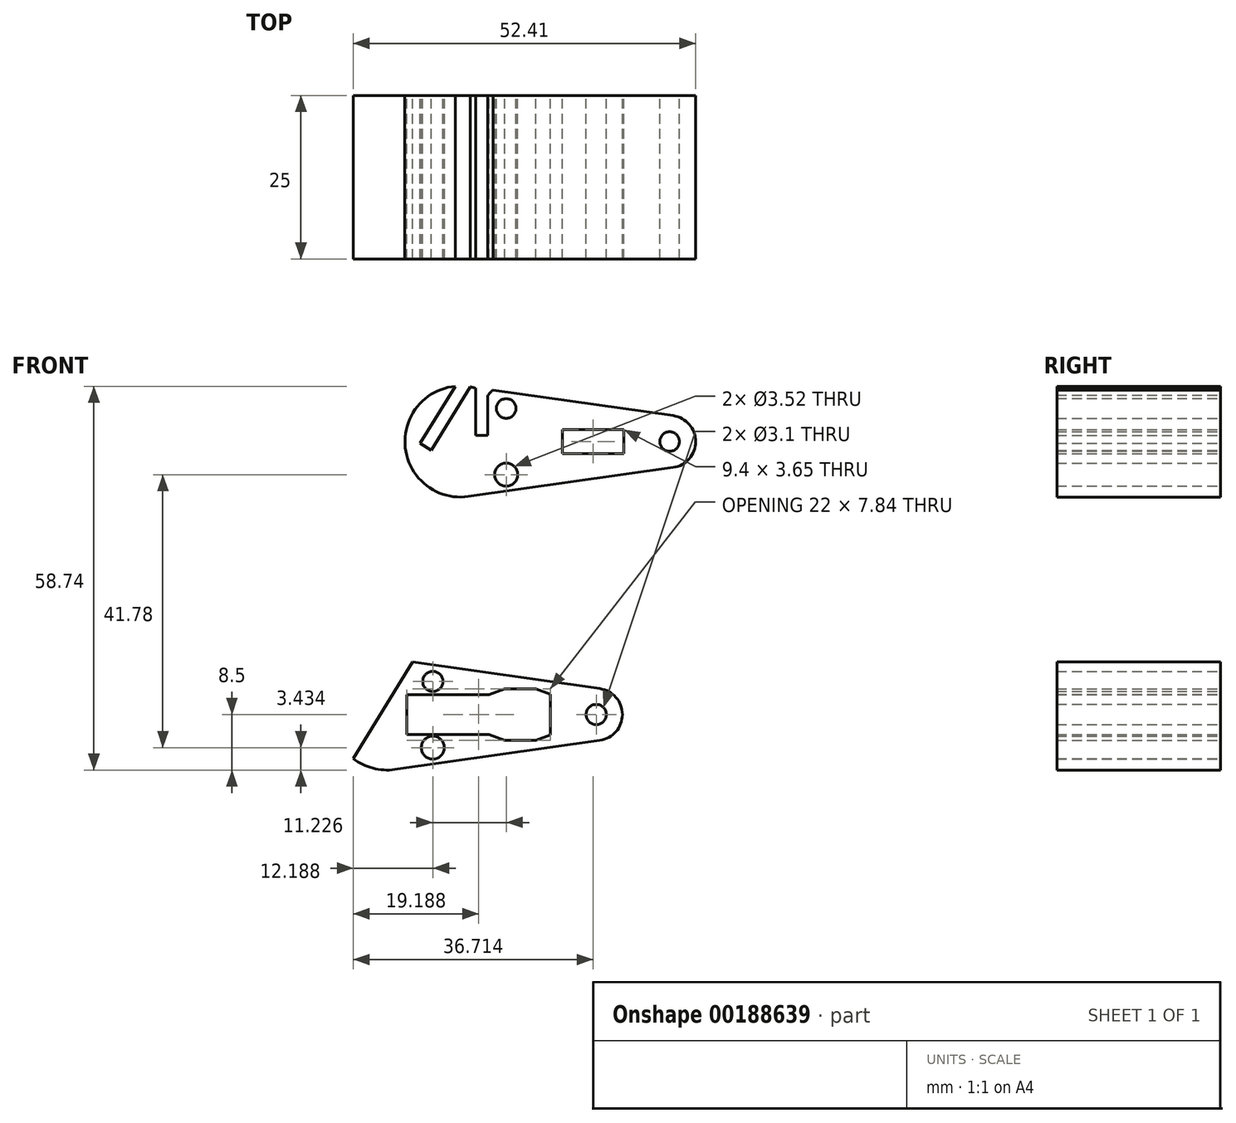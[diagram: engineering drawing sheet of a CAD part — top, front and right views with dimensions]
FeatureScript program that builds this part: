
annotation { "Feature Type Name" : "Feature", "Feature Type Description" : "" }
export const myFeature = defineFeature(function(context is Context, id is Id, definition is map)
    precondition{}
    {
        {
            var Q0;
            Q0=qCreatedBy(makeId("Front.planeOp"),FACE);
            var sketch = newSketch(context, id + "F0", { "sketchPlane" : qUnion([Q0])});
            skCircle(sketch, "E0", {"center": v(-54.37, 44.88) * mm, "radius": 8.5 * mm});
            skCircle(sketch, "E1", {"center": v(-22.37, 44.88) * mm, "radius": 4 * mm});
            skLineSegment(sketch, "E2", {"start": v(-53.17, 53.3) * mm, "end": v(-21.8, 48.84) * mm});
            skLineSegment(sketch, "E3", {"start": v(-53.17, 36.46) * mm, "end": v(-21.8, 40.92) * mm});
            skCircle(sketch, "E4", {"center": v(-22.37, 44.88) * mm, "radius": 1.5 * mm});
            skCircle(sketch, "E5", {"center": v(-47.37, 49.95) * mm, "radius": 1.5 * mm});
            skCircle(sketch, "E6", {"center": v(-47.37, 39.81) * mm, "radius": 1.76 * mm});
            skLineSegment(sketch, "E7", {"start": v(-47.56, 49.97) * mm, "end": v(-25.83, 46.89) * mm, "construction": true});
            skLineSegment(sketch, "E8", {"start": v(-47.56, 39.79) * mm, "end": v(-25.83, 42.87) * mm, "construction": true});
            skLineSegment(sketch, "E9", {"start": v(-47.37, 49.95) * mm, "end": v(-47.37, 39.81) * mm, "construction": true});
            skLineSegment(sketch, "E10.bottom", {"start": v(-38.77, 46.7) * mm, "end": v(-29.37, 46.7) * mm});
            skLineSegment(sketch, "E10.top", {"start": v(-38.77, 43.06) * mm, "end": v(-29.37, 43.06) * mm});
            skLineSegment(sketch, "E10.left", {"start": v(-38.77, 46.7) * mm, "end": v(-38.77, 43.06) * mm});
            skLineSegment(sketch, "E10.right", {"start": v(-29.37, 46.7) * mm, "end": v(-29.37, 43.06) * mm});
            skLineSegment(sketch, "E11.bottom", {"start": v(-52.07, 53.3) * mm, "end": v(-50.17, 53.3) * mm});
            skLineSegment(sketch, "E11.top", {"start": v(-52.07, 45.8) * mm, "end": v(-50.17, 45.8) * mm});
            skLineSegment(sketch, "E11.left", {"start": v(-52.07, 53.3) * mm, "end": v(-52.07, 45.8) * mm});
            skLineSegment(sketch, "E11.right", {"start": v(-50.17, 53.3) * mm, "end": v(-50.17, 45.8) * mm});
            skLineSegment(sketch, "E12", {"start": v(-58.83, 43.56) * mm, "end": v(-60.53, 44.6) * mm});
            skLineSegment(sketch, "E13", {"start": v(-60.53, 44.6) * mm, "end": v(-54.53, 54.34) * mm});
            skLineSegment(sketch, "E14", {"start": v(-47.37, 64.07) * mm, "end": v(-62.3, 39.81) * mm, "construction": true});
            skCircle(sketch, "E15", {"center": v(-65.6, 3.1) * mm, "radius": 8.5 * mm});
            skCircle(sketch, "E16", {"center": v(-33.6, 3.1) * mm, "radius": 4 * mm});
            skLineSegment(sketch, "E17", {"start": v(-64.4, 11.52) * mm, "end": v(-33.03, 7.06) * mm});
            skLineSegment(sketch, "E18", {"start": v(-64.4, -5.32) * mm, "end": v(-33.03, -0.86) * mm});
            skCircle(sketch, "E19", {"center": v(-33.6, 3.1) * mm, "radius": 1.55 * mm});
            skCircle(sketch, "E20", {"center": v(-58.6, 8.17) * mm, "radius": 1.55 * mm});
            skCircle(sketch, "E21", {"center": v(-58.6, -1.97) * mm, "radius": 1.76 * mm});
            skLineSegment(sketch, "E22", {"start": v(-58.79, 8.2) * mm, "end": v(-37.05, 5.1) * mm, "construction": true});
            skLineSegment(sketch, "E23", {"start": v(-58.79, -2) * mm, "end": v(-37.05, 1.1) * mm, "construction": true});
            skLineSegment(sketch, "E24", {"start": v(-58.6, 8.17) * mm, "end": v(-58.6, -1.97) * mm, "construction": true});
            skLineSegment(sketch, "E25.bottom", {"start": v(-50, 7.02) * mm, "end": v(-40.6, 7.02) * mm});
            skLineSegment(sketch, "E25.top", {"start": v(-50, -0.82) * mm, "end": v(-40.6, -0.82) * mm});
            skLineSegment(sketch, "E25.left", {"start": v(-50, 7.02) * mm, "end": v(-50, -0.82) * mm});
            skLineSegment(sketch, "E25.right", {"start": v(-40.6, 7.02) * mm, "end": v(-40.6, -0.82) * mm});
            skLineSegment(sketch, "E26", {"start": v(-58.6, 22.3) * mm, "end": v(-73.53, -1.97) * mm, "construction": true});
            skLineSegment(sketch, "E27", {"start": v(-61.68, 11.13) * mm, "end": v(-70.78, -3.64) * mm});
            skLineSegment(sketch, "E28.bottom", {"start": v(-62.6, 6.15) * mm, "end": v(-50, 6.15) * mm});
            skLineSegment(sketch, "E28.top", {"start": v(-62.6, 0.05) * mm, "end": v(-50, 0.05) * mm});
            skLineSegment(sketch, "E28.left", {"start": v(-62.6, 6.15) * mm, "end": v(-62.6, 0.05) * mm});
            skLineSegment(sketch, "E28.right", {"start": v(-50, 6.15) * mm, "end": v(-50, 0.05) * mm});
            skLineSegment(sketch, "E29", {"start": v(-50, 6.15) * mm, "end": v(-47.6, 7.02) * mm});
            skLineSegment(sketch, "E30", {"start": v(-42.84, 7.02) * mm, "end": v(-40.6, 6.2) * mm});
            skLineSegment(sketch, "E31", {"start": v(-50, 0.05) * mm, "end": v(-47.6, -0.82) * mm});
            skLineSegment(sketch, "E32", {"start": v(-40.6, 0) * mm, "end": v(-42.84, -0.82) * mm});
            skLineSegment(sketch, "E33", {"start": v(-58.83, 43.56) * mm, "end": v(-52.83, 53.3) * mm});
            skPoint(sketch, "E33.endSnap0", {"position": v(-52.83, 51.47) * mm});
            skLineSegment(sketch, "E34", {"start": v(-52.83, 53.3) * mm, "end": v(-54.53, 54.34) * mm});
            skCircle(sketch, "E35", {"center": v(-47.37, 49.95) * mm, "radius": 3.45 * mm});
            skCircle(sketch, "E36", {"center": v(-47.37, 39.81) * mm, "radius": 3.45 * mm});
            skCircle(sketch, "E37", {"center": v(-58.6, 8.17) * mm, "radius": 3 * mm});
            skCircle(sketch, "E38", {"center": v(-58.6, -1.97) * mm, "radius": 3.45 * mm});
            skSolve(sketch);
        }
        {
            var Q0;
            {var subQ0=sQuery(id+"F0.wireOp",EDGE,"E35");var subQ1=sQuery(id+"F0.wireOp",EDGE,"E2");var subQ2=makeQuery(id+"F0.imprint","INTERSECT",VERTEX,{"disambiguationData":[OD(0.0)],"derivedFrom":[subQ1,subQ0]});Q0=makeQuery(id+"F0.imprint","IMPRINT",FACE,{"disambiguationData":[TD([[makeQuery(id+"F0.imprint","IMPRINT",EDGE,{"disambiguationData":[TD([[subQ2,-1.0]])],"derivedFrom":subQ1}),1.0]])]});}
            var Q1;
            {var subQ0=sQuery(id+"F0.wireOp",EDGE,"E36");var subQ1=sQuery(id+"F0.wireOp",EDGE,"E3");var subQ2=makeQuery(id+"F0.imprint","INTERSECT",VERTEX,{"disambiguationData":[OD(0.0)],"derivedFrom":[subQ1,subQ0]});Q1=makeQuery(id+"F0.imprint","IMPRINT",FACE,{"disambiguationData":[TD([[makeQuery(id+"F0.imprint","IMPRINT",EDGE,{"disambiguationData":[TD([[subQ2,-1.0]])],"derivedFrom":subQ1}),-1.0]])]});}
            var Q2;
            {var subQ0=sQuery(id+"F0.wireOp",EDGE,"E37");var subQ1=sQuery(id+"F0.wireOp",EDGE,"E17");var subQ2=makeQuery(id+"F0.imprint","INTERSECT",VERTEX,{"disambiguationData":[OD(0.0)],"derivedFrom":[subQ1,subQ0]});Q2=makeQuery(id+"F0.imprint","IMPRINT",FACE,{"disambiguationData":[TD([[makeQuery(id+"F0.imprint","IMPRINT",EDGE,{"disambiguationData":[TD([[subQ2,-1.0]])],"derivedFrom":subQ1}),1.0]])]});}
            var Q3;
            {var subQ0=sQuery(id+"F0.wireOp",EDGE,"E38");var subQ1=sQuery(id+"F0.wireOp",EDGE,"E18");var subQ2=makeQuery(id+"F0.imprint","INTERSECT",VERTEX,{"disambiguationData":[OD(0.0)],"derivedFrom":[subQ1,subQ0]});Q3=makeQuery(id+"F0.imprint","IMPRINT",FACE,{"disambiguationData":[TD([[makeQuery(id+"F0.imprint","IMPRINT",EDGE,{"disambiguationData":[TD([[subQ2,-1.0]])],"derivedFrom":subQ1}),-1.0]])]});}
            var Q4;
            {var subQ0=sQuery(id+"F0.wireOp",EDGE,"E3");var subQ1=sQuery(id+"F0.wireOp",EDGE,"E0");var subQ2=makeQuery(id+"F0.imprint","INTERSECT",VERTEX,{"derivedFrom":[subQ1,subQ0]});Q4=makeQuery(id+"F0.imprint","IMPRINT",FACE,{"disambiguationData":[TD([[makeQuery(id+"F0.imprint","IMPRINT",EDGE,{"disambiguationData":[TD([[subQ2,-1.0]])],"derivedFrom":subQ1}),-1.0]])]});}
            var Q5;
            Q5=makeQuery(id+"F0.imprint","IMPRINT",FACE,{"disambiguationData":[TD([[makeQuery(id+"F0.imprint","IMPRINT",EDGE,{"derivedFrom":sQuery(id+"F0.wireOp",EDGE,"E4")}),-1.0]])]});
            var Q6;
            {var subQ0=sQuery(id+"F0.wireOp",EDGE,"E18");var subQ1=sQuery(id+"F0.wireOp",EDGE,"E15");var subQ2=makeQuery(id+"F0.imprint","INTERSECT",VERTEX,{"derivedFrom":[subQ1,subQ0]});Q6=makeQuery(id+"F0.imprint","IMPRINT",FACE,{"disambiguationData":[TD([[makeQuery(id+"F0.imprint","IMPRINT",EDGE,{"disambiguationData":[TD([[subQ2,-1.0]])],"derivedFrom":subQ1}),-1.0]])]});}
            var Q7;
            Q7=makeQuery(id+"F0.imprint","IMPRINT",FACE,{"disambiguationData":[TD([[makeQuery(id+"F0.imprint","IMPRINT",EDGE,{"derivedFrom":sQuery(id+"F0.wireOp",EDGE,"E19")}),-1.0]])]});
            var Q8;
            {var subQ0=sQuery(id+"F0.wireOp",EDGE,"E37");var subQ1=sQuery(id+"F0.wireOp",EDGE,"E15");var subQ2=makeQuery(id+"F0.imprint","INTERSECT",VERTEX,{"disambiguationData":[OD(1.0)],"derivedFrom":[subQ1,subQ0]});Q8=makeQuery(id+"F0.imprint","IMPRINT",FACE,{"disambiguationData":[TD([[makeQuery(id+"F0.imprint","IMPRINT",EDGE,{"disambiguationData":[TD([[subQ2,-1.0]])],"derivedFrom":subQ1}),-1.0]])]});}
            var Q9;
            {var subQ0=sQuery(id+"F0.wireOp",EDGE,"E5");var subQ1=sQuery(id+"F0.wireOp",EDGE,"E0");var subQ2=makeQuery(id+"F0.imprint","INTERSECT",VERTEX,{"disambiguationData":[OD(0.0)],"derivedFrom":[subQ1,subQ0]});Q9=makeQuery(id+"F0.imprint","IMPRINT",FACE,{"disambiguationData":[TD([[makeQuery(id+"F0.imprint","IMPRINT",EDGE,{"disambiguationData":[TD([[subQ2,1.0]])],"derivedFrom":subQ1}),-1.0]])]});}
            var Q10;
            {var subQ0=sQuery(id+"F0.wireOp",EDGE,"E36");var subQ5=sQuery(id+"F0.wireOp",EDGE,"E0");var subQ9=makeQuery(id+"F0.imprint","INTERSECT",VERTEX,{"disambiguationData":[OD(0.0)],"derivedFrom":[subQ5,subQ0]});Q10=makeQuery(id+"F0.imprint","IMPRINT",FACE,{"disambiguationData":[TD([[makeQuery(id+"F0.imprint","IMPRINT",EDGE,{"disambiguationData":[TD([[subQ9,-1.0]])],"derivedFrom":subQ5}),-1.0]])]});}
            var Q11;
            Q11=makeQuery(id+"F0.imprint","IMPRINT",FACE,{"disambiguationData":[TD([[makeQuery(id+"F0.imprint","IMPRINT",EDGE,{"derivedFrom":sQuery(id+"F0.wireOp",EDGE,"E10.bottom")}),1.0]])]});
            var Q12;
            {var subQ1=sQuery(id+"F0.wireOp",EDGE,"E15");var subQ9=sQuery(id+"F0.wireOp",EDGE,"E28.bottom");var subQ11=makeQuery(id+"F0.imprint","INTERSECT",VERTEX,{"derivedFrom":[subQ1,subQ9]});Q12=makeQuery(id+"F0.imprint","IMPRINT",FACE,{"disambiguationData":[TD([[makeQuery(id+"F0.imprint","IMPRINT",EDGE,{"disambiguationData":[TD([[subQ11,-1.0]])],"derivedFrom":subQ1}),-1.0]])]});}
            var Q13;
            {var subQ11=sQuery(id+"F0.wireOp",EDGE,"E28.left");Q13=makeQuery(id+"F0.imprint","IMPRINT",FACE,{"disambiguationData":[TD([[makeQuery(id+"F0.imprint","IMPRINT",EDGE,{"derivedFrom":subQ11}),-1.0]])]});}
            var Q14;
            {var subQ0=sQuery(id+"F0.wireOp",EDGE,"E38");var subQ5=sQuery(id+"F0.wireOp",EDGE,"E15");var subQ11=makeQuery(id+"F0.imprint","INTERSECT",VERTEX,{"disambiguationData":[OD(0.0)],"derivedFrom":[subQ5,subQ0]});Q14=makeQuery(id+"F0.imprint","IMPRINT",FACE,{"disambiguationData":[TD([[makeQuery(id+"F0.imprint","IMPRINT",EDGE,{"disambiguationData":[TD([[subQ11,-1.0]])],"derivedFrom":subQ5}),-1.0]])]});}
            var Q15;
            {var subQ6=sQuery(id+"F0.wireOp",EDGE,"E11.top");Q15=makeQuery(id+"F0.imprint","IMPRINT",FACE,{"disambiguationData":[TD([[makeQuery(id+"F0.imprint","IMPRINT",EDGE,{"derivedFrom":subQ6}),-1.0]])]});}
            var Q16;
            {var subQ13=sQuery(id+"F0.wireOp",EDGE,"E17");var subQ28=sQuery(id+"F0.wireOp",EDGE,"E16");var subQ31=makeQuery(id+"F0.imprint","INTERSECT",VERTEX,{"derivedFrom":[subQ28,subQ13]});Q16=makeQuery(id+"F0.imprint","IMPRINT",FACE,{"disambiguationData":[TD([[makeQuery(id+"F0.imprint","IMPRINT",EDGE,{"disambiguationData":[TD([[subQ31,-1.0]])],"derivedFrom":subQ28}),-1.0]])]});}
            var Q17;
            {var subQ4=sQuery(id+"F0.wireOp",EDGE,"E5");var subQ5=sQuery(id+"F0.wireOp",EDGE,"E0");var subQ6=makeQuery(id+"F0.imprint","INTERSECT",VERTEX,{"disambiguationData":[OD(0.0)],"derivedFrom":[subQ5,subQ4]});Q17=makeQuery(id+"F0.imprint","IMPRINT",FACE,{"disambiguationData":[TD([[makeQuery(id+"F0.imprint","IMPRINT",EDGE,{"disambiguationData":[TD([[subQ6,1.0]])],"derivedFrom":subQ5}),1.0]])]});}
            var Q18;
            {var subQ0=sQuery(id+"F0.wireOp",EDGE,"E36");var subQ1=sQuery(id+"F0.wireOp",EDGE,"E0");var subQ2=makeQuery(id+"F0.imprint","INTERSECT",VERTEX,{"disambiguationData":[OD(0.0)],"derivedFrom":[subQ1,subQ0]});Q18=makeQuery(id+"F0.imprint","IMPRINT",FACE,{"disambiguationData":[TD([[makeQuery(id+"F0.imprint","IMPRINT",EDGE,{"disambiguationData":[TD([[subQ2,-1.0]])],"derivedFrom":subQ1}),1.0]])]});}
            var Q19;
            {var subQ1=sQuery(id+"F0.wireOp",EDGE,"E15");var subQ3=sQuery(id+"F0.wireOp",EDGE,"E38");var subQ5=makeQuery(id+"F0.imprint","INTERSECT",VERTEX,{"disambiguationData":[OD(0.0)],"derivedFrom":[subQ1,subQ3]});Q19=makeQuery(id+"F0.imprint","IMPRINT",FACE,{"disambiguationData":[TD([[makeQuery(id+"F0.imprint","IMPRINT",EDGE,{"disambiguationData":[TD([[subQ5,-1.0]])],"derivedFrom":subQ1}),1.0]])]});}
            var Q20;
            {var subQ0=sQuery(id+"F0.wireOp",EDGE,"E28.bottom");var subQ1=sQuery(id+"F0.wireOp",EDGE,"E15");var subQ2=makeQuery(id+"F0.imprint","INTERSECT",VERTEX,{"derivedFrom":[subQ1,subQ0]});Q20=makeQuery(id+"F0.imprint","IMPRINT",FACE,{"disambiguationData":[TD([[makeQuery(id+"F0.imprint","IMPRINT",EDGE,{"disambiguationData":[TD([[subQ2,-1.0]])],"derivedFrom":subQ1}),1.0]])]});}
            var Q21;
            {var subQ3=sQuery(id+"F0.wireOp",EDGE,"E32");Q21=makeQuery(id+"F0.imprint","IMPRINT",FACE,{"disambiguationData":[TD([[makeQuery(id+"F0.imprint","IMPRINT",EDGE,{"derivedFrom":subQ3}),1.0]])]});}
            var Q22;
            {var subQ3=sQuery(id+"F0.wireOp",EDGE,"E31");Q22=makeQuery(id+"F0.imprint","IMPRINT",FACE,{"disambiguationData":[TD([[makeQuery(id+"F0.imprint","IMPRINT",EDGE,{"derivedFrom":subQ3}),-1.0]])]});}
            var Q23;
            {var subQ3=sQuery(id+"F0.wireOp",EDGE,"E30");Q23=makeQuery(id+"F0.imprint","IMPRINT",FACE,{"disambiguationData":[TD([[makeQuery(id+"F0.imprint","IMPRINT",EDGE,{"derivedFrom":subQ3}),1.0]])]});}
            var Q24;
            {var subQ3=sQuery(id+"F0.wireOp",EDGE,"E29");Q24=makeQuery(id+"F0.imprint","IMPRINT",FACE,{"disambiguationData":[TD([[makeQuery(id+"F0.imprint","IMPRINT",EDGE,{"derivedFrom":subQ3}),1.0]])]});}
            extrude(context, id + "F1", {"entities" : qUnion([Q0, Q1, Q2, Q3, Q4, Q5, Q6, Q7, Q8, Q9, Q10, Q11, Q12, Q13, Q14, Q15, Q16, Q17, Q18, Q19, Q20, Q21, Q22, Q23, Q24]), "depth" : 25 * mm});
        }
    });
